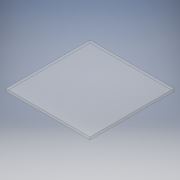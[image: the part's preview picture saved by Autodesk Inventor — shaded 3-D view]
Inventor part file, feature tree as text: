
AUTODESK INVENTOR PART (.ipt)
format: ipt  version: 2019 (Build 230136000, 136)  size: 94,720 bytes
history: native  units: in
note: dims shown in document units (in); Inventor stores cm internally (conversion verified against a paired STEP export)
features: extrude x1, sketch x1
ambient origin geometry x8: Origin, YZ Plane, XZ Plane, XY Plane, X Axis, Y Axis, Z Axis, Center Point
bodies: Solid1 (feature_tree)
feature tree (2):
  extrude  "Extrusion1"  Depth=4.0in
  sketch  "Sketch1"  dims[d0=4.0in d1=4.0in d2=0.125in d3=0.0in]
